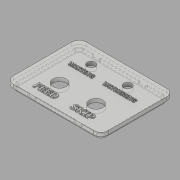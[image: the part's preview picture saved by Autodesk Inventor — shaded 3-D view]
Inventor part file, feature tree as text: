
AUTODESK INVENTOR PART (.ipt)
format: ipt  version: 2017 (Build 210142000, 142)  size: 535,552 bytes
history: native  units: mm
features: sketch x6, extrude x5, thicken_offset x2, other x2
ambient origin geometry x8: Origin, YZ Plane, XZ Plane, XY Plane, X Axis, Y Axis, Z Axis, Center Point
bodies: Solid1 (feature_tree)
feature tree (15):
  extrude  "Lid Surface Top"  Depth=3.0mm TaperAngle=0.0deg
  thicken_offset  "Thicken1"
  thicken_offset  "Thicken2"
  extrude  "Bottom Lip Notches"  Depth=4.0mm
  extrude  "Top Lip Notches"  Depth=1.0mm
  extrude  "LED/Button Holes"  Depth=1.0mm TaperAngle=0.0deg
  extrude  "Text"  Depth=6.5mm
  sketch  "Sketch1"  dims[d0=4.0mm d1=3.0mm d2=0.0mm]
  sketch  "Sketch2"  dims[d3=2.0mm d4=1.5mm d5=4.0mm]
  other  "Srf1"
  sketch  "Sketch3"  dims[d6=3.0mm d7=0.0mm d8=1.0mm]
  sketch  "Sketch4"  dims[d9=1.0mm d10=1.0mm d11=0.0mm]
  sketch  "Sketch5"  dims[d12=1.0mm d13=0.0mm d14=6.5mm d15=6.5mm d16=11.0mm d17=11.0mm]
  other  "Inside Lip"
  sketch  "Sketch6"  dims[d18=3.0mm d19=0.0mm d20=0.0mm d21=0.1mm d23=0.0mm d24=0.75mm]
